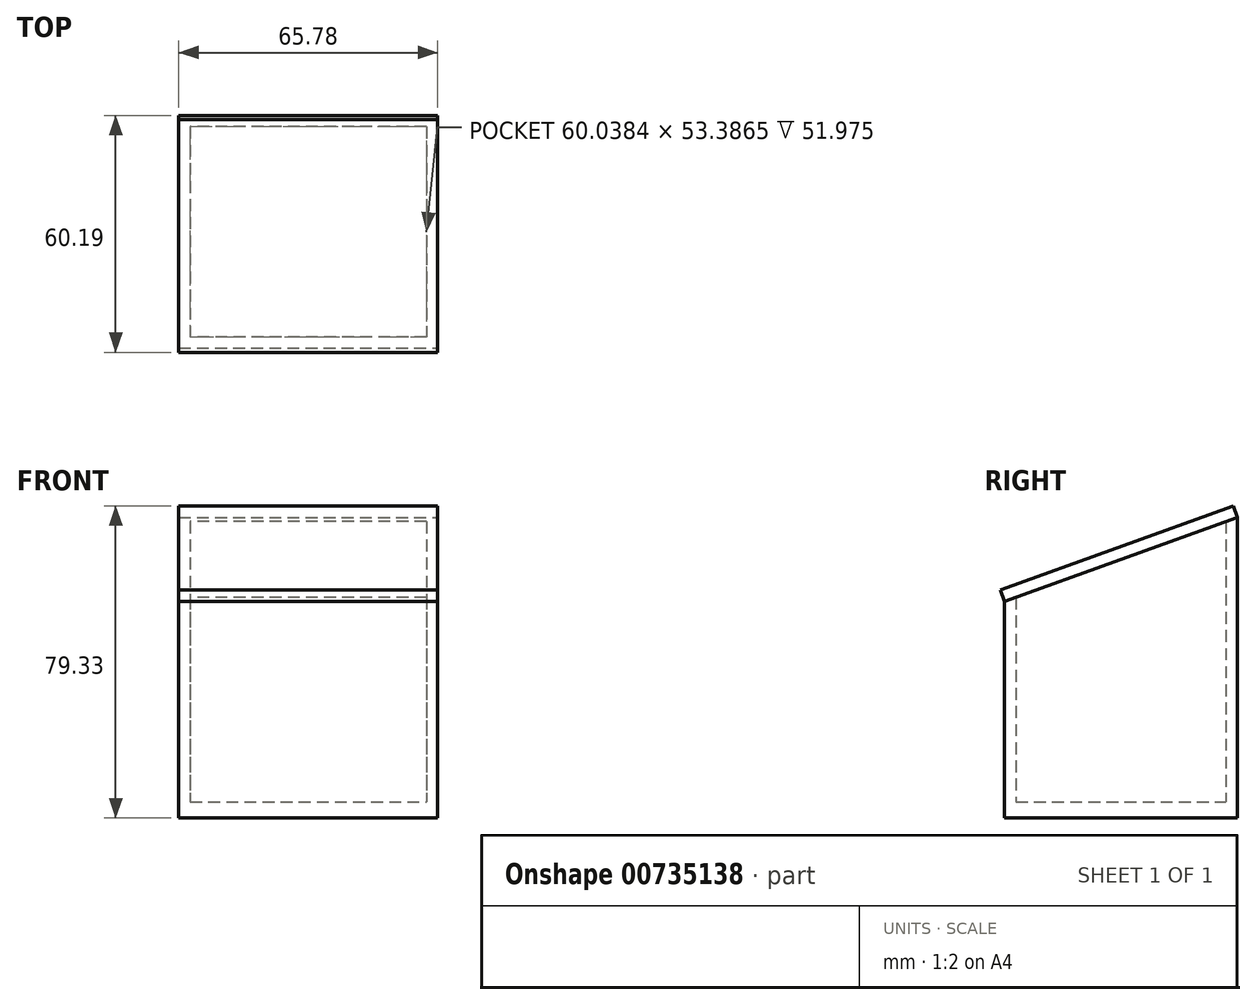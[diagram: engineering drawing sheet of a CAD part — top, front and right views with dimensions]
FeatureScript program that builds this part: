
annotation { "Feature Type Name" : "Feature", "Feature Type Description" : "" }
export const myFeature = defineFeature(function(context is Context, id is Id, definition is map)
    precondition{}
    {
        {
            var Q0;
            Q0=qCreatedBy(makeId("Top.planeOp"),FACE);
            var sketch = newSketch(context, id + "F0", { "sketchPlane" : qUnion([Q0])});
            skLineSegment(sketch, "E0.bottom", {"start": v(0, 0) * mm, "end": v(65.78, 0) * mm});
            skLineSegment(sketch, "E0.top", {"start": v(0, 59.13) * mm, "end": v(65.78, 59.13) * mm});
            skLineSegment(sketch, "E0.left", {"start": v(0, 0) * mm, "end": v(0, 59.13) * mm});
            skLineSegment(sketch, "E0.right", {"start": v(65.78, 0) * mm, "end": v(65.78, 59.13) * mm});
            skSolve(sketch);
        }
        {
            var Q0;
            Q0 = qSketchRegion(id + "F0", true);
            extrude(context, id + "F1", {"entities" : qUnion([Q0]), "depth" : 4.06 * mm, "offsetDistance" : 25.4 * mm});
        }
        {
            var Q0;
            Q0=makeQuery(id+"F1.opExtrude","CAP_FACE",FACE,{"disambiguationData":[OSD([sQuery(id+"F0.wireOp",EDGE,"E0.bottom"),sQuery(id+"F0.wireOp",EDGE,"E0.top"),sQuery(id+"F0.wireOp",EDGE,"E0.left"),sQuery(id+"F0.wireOp",EDGE,"E0.right")])],"isStart":false});
            var sketch = newSketch(context, id + "F2", { "sketchPlane" : qUnion([Q0])});
            skSolve(sketch);
        }
        {
            var Q0;
            Q0=makeQuery(id+"F2.imprint","IMPRINT",FACE,{"disambiguationData":[TD([[makeQuery(id+"F2.imprint","IMPRINT",EDGE,{"derivedFrom":makeQuery(id+"F1.opExtrude","CAP_EDGE",EDGE,{"disambiguationData":[OSD([sQuery(id+"F0.wireOp",EDGE,"E0.bottom")])],"isStart":false})}),1.0]])]});
            var sketch = newSketch(context, id + "F3", { "sketchPlane" : qUnion([Q0])});
            skLineSegment(sketch, "E1.0", {"start": v(2.87, 2.87) * mm, "end": v(62.9, 2.87) * mm});
            skLineSegment(sketch, "E1.1", {"start": v(2.87, 2.87) * mm, "end": v(2.87, 56.26) * mm});
            skLineSegment(sketch, "E1.2", {"start": v(2.87, 56.26) * mm, "end": v(62.9, 56.26) * mm});
            skLineSegment(sketch, "E1.3", {"start": v(62.9, 2.87) * mm, "end": v(62.9, 56.26) * mm});
            skSolve(sketch);
        }
        {
            var Q0;
            Q0=makeQuery(id+"F3.imprint","IMPRINT",FACE,{"disambiguationData":[TD([[makeQuery(id+"F3.imprint","IMPRINT",EDGE,{"derivedFrom":sQuery(id+"F3.wireOp",EDGE,"E1.0")}),-1.0]])]});
            extrude(context, id + "F4", {"entities" : qUnion([Q0]), "operationType" : NewBodyOperationType.ADD, "depth" : 72.34 * mm, "offsetDistance" : 25.4 * mm});
        }
        {
            var Q0;
            {var subQ0=sQuery(id+"F0.wireOp",EDGE,"E0.right");Q0=makeQuery(id+"F4.boolean.opBoolean","MERGE",FACE,{"derivedFrom":[makeQuery(id+"F1.opExtrude","SWEPT_FACE",FACE,{"disambiguationData":[OSD([subQ0])]}),makeQuery(id+"F4.opExtrude","SWEPT_FACE",FACE,{"disambiguationData":[OSD([subQ0])]})]});}
            var sketch = newSketch(context, id + "F5", { "sketchPlane" : qUnion([Q0])});
            skLineSegment(sketch, "E2", {"start": v(0, 55) * mm, "end": v(59.13, 76.4) * mm});
            skLineSegment(sketch, "E3", {"start": v(59.13, 76.4) * mm, "end": v(0, 76.4) * mm});
            skLineSegment(sketch, "E4", {"start": v(0, 76.4) * mm, "end": v(0, 55) * mm});
            skSolve(sketch);
        }
        {
            var Q0;
            Q0 = qSketchRegion(id + "F5", true);
            var Q1;
            {var subQ0=sQuery(id+"F0.wireOp",EDGE,"E0.left");Q1=makeQuery(id+"F4.boolean.opBoolean","MERGE",FACE,{"derivedFrom":[makeQuery(id+"F1.opExtrude","SWEPT_FACE",FACE,{"disambiguationData":[OSD([subQ0])]}),makeQuery(id+"F4.opExtrude","SWEPT_FACE",FACE,{"disambiguationData":[OSD([subQ0])]})]});}
            extrude(context, id + "F6", {"entities" : qUnion([Q0]), "operationType" : NewBodyOperationType.REMOVE, "endBound" : BoundingType.UP_TO_SURFACE, "oppositeDirection" : true, "depth" : 25.4 * mm, "endBoundEntityFace" : qUnion([Q1]), "offsetDistance" : 25.4 * mm});
        }
        {
            var Q0;
            Q0=makeQuery(id+"F6.boolean.opBoolean","COPY",FACE,{"derivedFrom":makeQuery(id+"F6.opExtrude","SWEPT_FACE",FACE,{"disambiguationData":[OSD([sQuery(id+"F5.wireOp",EDGE,"E2")])]})});
            var sketch = newSketch(context, id + "F7", { "sketchPlane" : qUnion([Q0])});
            skLineSegment(sketch, "E5.bottom", {"start": v(0, 18.72) * mm, "end": v(65.78, 18.72) * mm});
            skLineSegment(sketch, "E5.top", {"start": v(0, 81.6) * mm, "end": v(65.78, 81.6) * mm});
            skLineSegment(sketch, "E5.left", {"start": v(0, 18.72) * mm, "end": v(0, 81.6) * mm});
            skLineSegment(sketch, "E5.right", {"start": v(65.78, 18.72) * mm, "end": v(65.78, 81.6) * mm});
            skSolve(sketch);
        }
        {
            var Q0;
            Q0 = qSketchRegion(id + "F7", true);
            extrude(context, id + "F8", {"entities" : qUnion([Q0]), "depth" : 3.1 * mm, "offsetDistance" : 25.4 * mm});
        }
    });
